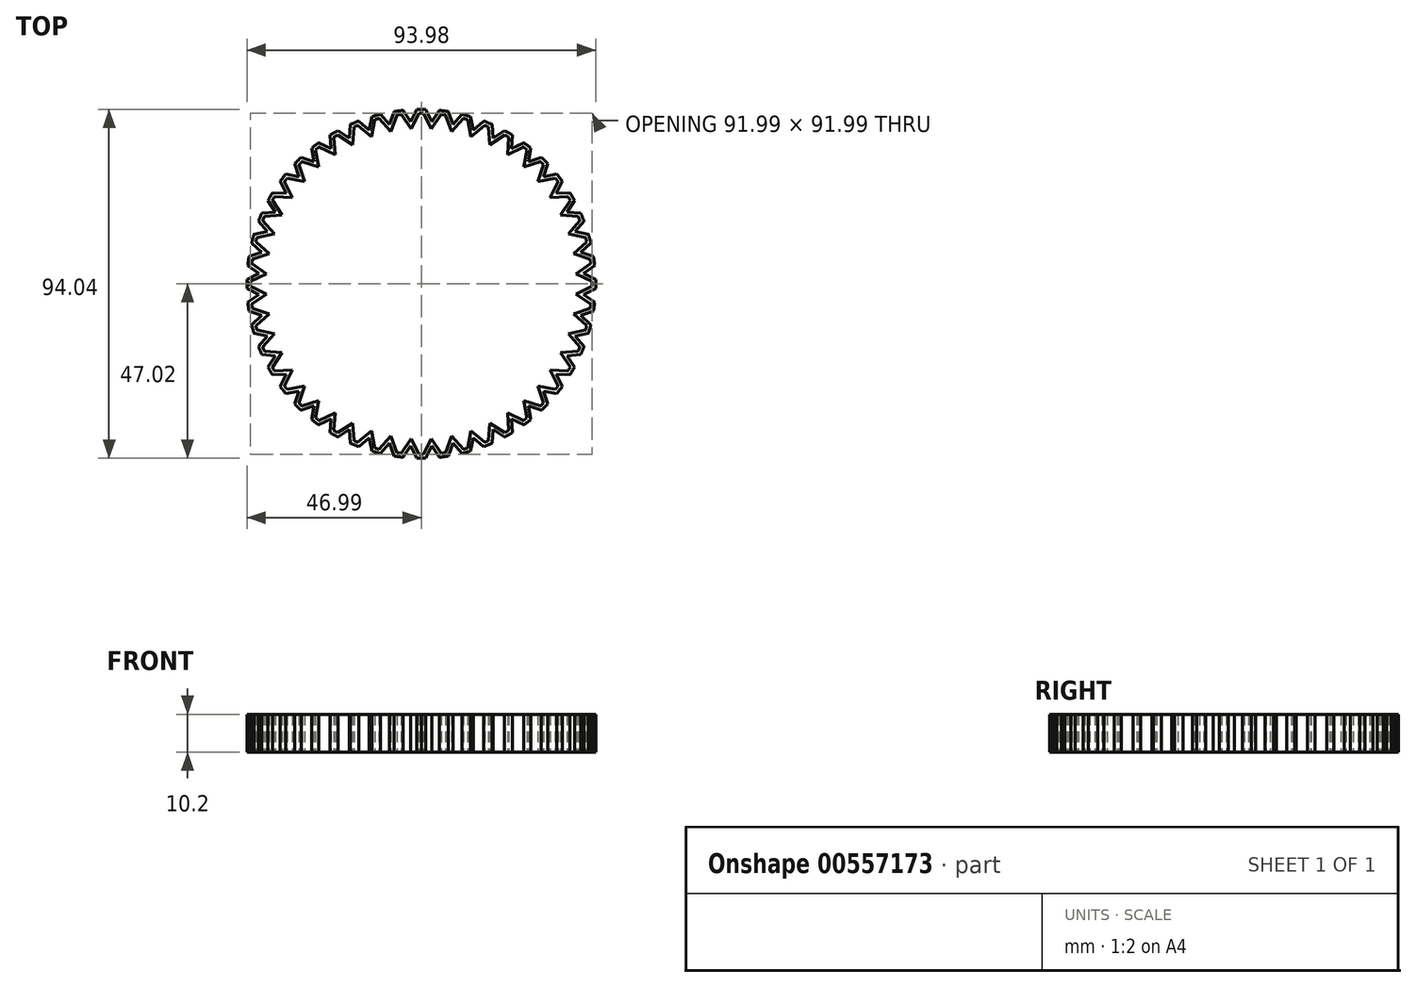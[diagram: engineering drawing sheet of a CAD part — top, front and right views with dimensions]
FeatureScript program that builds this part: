
annotation { "Feature Type Name" : "Feature", "Feature Type Description" : "" }
export const myFeature = defineFeature(function(context is Context, id is Id, definition is map)
    precondition{}
    {
        {
            var Q0;
            Q0=qCreatedBy(makeId("Top.planeOp"),FACE);
            var sketch = newSketch(context, id + "F0", { "sketchPlane" : qUnion([Q0])});
            skLineSegment(sketch, "E0", {"start": v(-43.7, 2.86) * mm, "end": v(-46.74, 4.94) * mm});
            skLineSegment(sketch, "E1", {"start": v(-46.99, 1.2) * mm, "end": v(-43.7, 2.86) * mm});
            skArc(sketch, "E2", {"start": v(-4.94, 46.74) * mm, "mid": v(-6.13, 46.6) * mm, "end": v(-7.33, 46.43) * mm});
            skArc(sketch, "E3", {"start": v(-11, 45.7) * mm, "mid": v(-12.16, 45.4) * mm, "end": v(-13.33, 45.07) * mm});
            skArc(sketch, "E4", {"start": v(-16.86, 43.87) * mm, "mid": v(-17.99, 43.42) * mm, "end": v(-19.1, 42.95) * mm});
            skArc(sketch, "E5", {"start": v(-22.45, 41.3) * mm, "mid": v(-23.5, 40.7) * mm, "end": v(-24.54, 40.09) * mm});
            skArc(sketch, "E6", {"start": v(-27.64, 38.01) * mm, "mid": v(-28.61, 37.29) * mm, "end": v(-29.56, 36.54) * mm});
            skLineSegment(sketch, "E7", {"start": v(-40.09, 24.54) * mm, "end": v(-36.42, 24.33) * mm});
            skLineSegment(sketch, "E8", {"start": v(-39.28, 19.37) * mm, "end": v(-41.3, 22.45) * mm});
            skLineSegment(sketch, "E9", {"start": v(-42.95, 19.1) * mm, "end": v(-39.28, 19.37) * mm});
            skLineSegment(sketch, "E10", {"start": v(-41.48, 14.08) * mm, "end": v(-43.87, 16.86) * mm});
            skLineSegment(sketch, "E11", {"start": v(-45.07, 13.33) * mm, "end": v(-41.48, 14.08) * mm});
            skLineSegment(sketch, "E12", {"start": v(-42.96, 8.55) * mm, "end": v(-45.7, 11) * mm});
            skLineSegment(sketch, "E13", {"start": v(-46.43, 7.33) * mm, "end": v(-42.96, 8.55) * mm});
            skLineSegment(sketch, "E14", {"start": v(-36.42, 24.33) * mm, "end": v(-38.01, 27.64) * mm});
            skLineSegment(sketch, "E15", {"start": v(-36.54, 29.56) * mm, "end": v(-32.93, 28.88) * mm});
            skLineSegment(sketch, "E16", {"start": v(-32.93, 28.88) * mm, "end": v(-34.08, 32.37) * mm});
            skLineSegment(sketch, "E17", {"start": v(-28.88, 32.93) * mm, "end": v(-32.37, 34.08) * mm});
            skLineSegment(sketch, "E18", {"start": v(-28.88, 32.93) * mm, "end": v(-29.56, 36.54) * mm});
            skLineSegment(sketch, "E19", {"start": v(-24.33, 36.42) * mm, "end": v(-27.64, 38.01) * mm});
            skLineSegment(sketch, "E20", {"start": v(-24.33, 36.42) * mm, "end": v(-24.54, 40.09) * mm});
            skLineSegment(sketch, "E21", {"start": v(-19.37, 39.28) * mm, "end": v(-22.45, 41.3) * mm});
            skLineSegment(sketch, "E22", {"start": v(-19.37, 39.28) * mm, "end": v(-19.1, 42.95) * mm});
            skLineSegment(sketch, "E23", {"start": v(-14.08, 41.48) * mm, "end": v(-16.86, 43.87) * mm});
            skLineSegment(sketch, "E24", {"start": v(-14.08, 41.48) * mm, "end": v(-13.33, 45.07) * mm});
            skLineSegment(sketch, "E25", {"start": v(-8.55, 42.96) * mm, "end": v(-11, 45.7) * mm});
            skLineSegment(sketch, "E26", {"start": v(-8.55, 42.96) * mm, "end": v(-7.33, 46.43) * mm});
            skLineSegment(sketch, "E27", {"start": v(-2.86, 43.7) * mm, "end": v(-4.94, 46.74) * mm});
            skLineSegment(sketch, "E28", {"start": v(-2.86, 43.7) * mm, "end": v(-1.2, 46.99) * mm});
            skArc(sketch, "E29", {"start": v(-46.43, 7.33) * mm, "mid": v(-46.6, 6.13) * mm, "end": v(-46.74, 4.94) * mm});
            skArc(sketch, "E30", {"start": v(-45.07, 13.33) * mm, "mid": v(-45.4, 12.16) * mm, "end": v(-45.7, 11) * mm});
            skArc(sketch, "E31", {"start": v(-42.95, 19.1) * mm, "mid": v(-43.42, 17.99) * mm, "end": v(-43.87, 16.86) * mm});
            skArc(sketch, "E32", {"start": v(-40.09, 24.54) * mm, "mid": v(-40.7, 23.5) * mm, "end": v(-41.3, 22.45) * mm});
            skArc(sketch, "E33", {"start": v(-36.54, 29.56) * mm, "mid": v(-37.29, 28.61) * mm, "end": v(-38.01, 27.64) * mm});
            skArc(sketch, "E34", {"start": v(-32.37, 34.08) * mm, "mid": v(-33.23, 33.23) * mm, "end": v(-34.08, 32.37) * mm});
            skLineSegment(sketch, "E35.0", {"start": v(-2.74, 41.75) * mm, "end": v(-0.59, 46) * mm});
            skLineSegment(sketch, "E35.1", {"start": v(-2.74, 41.75) * mm, "end": v(-5.42, 45.68) * mm});
            skArc(sketch, "E35.2", {"start": v(-5.42, 45.68) * mm, "mid": v(-6, 45.6) * mm, "end": v(-6.59, 45.53) * mm});
            skLineSegment(sketch, "E35.3", {"start": v(-8.16, 41.03) * mm, "end": v(-6.59, 45.53) * mm});
            skLineSegment(sketch, "E35.4", {"start": v(-8.16, 41.03) * mm, "end": v(-11.34, 44.58) * mm});
            skArc(sketch, "E35.5", {"start": v(-11.34, 44.58) * mm, "mid": v(-11.9, 44.43) * mm, "end": v(-12.47, 44.28) * mm});
            skLineSegment(sketch, "E35.6", {"start": v(-13.45, 39.61) * mm, "end": v(-12.47, 44.28) * mm});
            skLineSegment(sketch, "E35.7", {"start": v(-13.45, 39.61) * mm, "end": v(-17.06, 42.72) * mm});
            skArc(sketch, "E35.8", {"start": v(-17.06, 42.72) * mm, "mid": v(-17.6, 42.5) * mm, "end": v(-18.14, 42.27) * mm});
            skLineSegment(sketch, "E35.9", {"start": v(-18.5, 37.52) * mm, "end": v(-18.14, 42.27) * mm});
            skLineSegment(sketch, "E35.10", {"start": v(-18.5, 37.52) * mm, "end": v(-22.5, 40.13) * mm});
            skArc(sketch, "E35.11", {"start": v(-22.5, 40.13) * mm, "mid": v(-23, 39.84) * mm, "end": v(-23.5, 39.54) * mm});
            skLineSegment(sketch, "E35.12", {"start": v(-23.24, 34.78) * mm, "end": v(-23.5, 39.54) * mm});
            skLineSegment(sketch, "E35.13", {"start": v(-42.27, 18.14) * mm, "end": v(-37.52, 18.5) * mm});
            skArc(sketch, "E35.14", {"start": v(-42.27, 18.14) * mm, "mid": v(-42.5, 17.6) * mm, "end": v(-42.72, 17.06) * mm});
            skLineSegment(sketch, "E35.15", {"start": v(-39.61, 13.45) * mm, "end": v(-42.72, 17.06) * mm});
            skLineSegment(sketch, "E35.16", {"start": v(-44.28, 12.47) * mm, "end": v(-39.61, 13.45) * mm});
            skArc(sketch, "E35.17", {"start": v(-44.28, 12.47) * mm, "mid": v(-44.43, 11.9) * mm, "end": v(-44.58, 11.34) * mm});
            skLineSegment(sketch, "E35.18", {"start": v(-41.03, 8.16) * mm, "end": v(-44.58, 11.34) * mm});
            skLineSegment(sketch, "E35.19", {"start": v(-46, 0.59) * mm, "end": v(-41.75, 2.74) * mm});
            skLineSegment(sketch, "E35.20", {"start": v(-41.75, 2.74) * mm, "end": v(-45.68, 5.42) * mm});
            skArc(sketch, "E35.21", {"start": v(-45.53, 6.59) * mm, "mid": v(-45.6, 6) * mm, "end": v(-45.68, 5.42) * mm});
            skLineSegment(sketch, "E35.22", {"start": v(-45.53, 6.59) * mm, "end": v(-41.03, 8.16) * mm});
            skLineSegment(sketch, "E35.23", {"start": v(-37.52, 18.5) * mm, "end": v(-40.13, 22.5) * mm});
            skArc(sketch, "E35.24", {"start": v(-39.54, 23.5) * mm, "mid": v(-39.84, 23) * mm, "end": v(-40.13, 22.5) * mm});
            skLineSegment(sketch, "E35.25", {"start": v(-39.54, 23.5) * mm, "end": v(-34.78, 23.24) * mm});
            skLineSegment(sketch, "E35.26", {"start": v(-34.78, 23.24) * mm, "end": v(-36.85, 27.54) * mm});
            skArc(sketch, "E35.27", {"start": v(-36.13, 28.47) * mm, "mid": v(-36.5, 28) * mm, "end": v(-36.85, 27.54) * mm});
            skLineSegment(sketch, "E35.28", {"start": v(-36.13, 28.47) * mm, "end": v(-31.45, 27.58) * mm});
            skLineSegment(sketch, "E35.29", {"start": v(-31.45, 27.58) * mm, "end": v(-32.94, 32.1) * mm});
            skArc(sketch, "E35.30", {"start": v(-32.1, 32.94) * mm, "mid": v(-32.53, 32.53) * mm, "end": v(-32.94, 32.1) * mm});
            skLineSegment(sketch, "E35.31", {"start": v(-27.58, 31.45) * mm, "end": v(-32.1, 32.94) * mm});
            skLineSegment(sketch, "E35.32", {"start": v(-27.58, 31.45) * mm, "end": v(-28.47, 36.13) * mm});
            skArc(sketch, "E35.33", {"start": v(-27.54, 36.85) * mm, "mid": v(-28, 36.5) * mm, "end": v(-28.47, 36.13) * mm});
            skLineSegment(sketch, "E35.34", {"start": v(-23.24, 34.78) * mm, "end": v(-27.54, 36.85) * mm});
            skLineSegment(sketch, "E36", {"start": v(-0.59, 46) * mm, "end": v(0, 46) * mm});
            skLineSegment(sketch, "E37", {"start": v(-1.2, 46.99) * mm, "end": v(0, 47.02) * mm});
            skLineSegment(sketch, "E38", {"start": v(-46, 0.59) * mm, "end": v(-46, 0) * mm});
            skLineSegment(sketch, "E39", {"start": v(-46.99, 1.2) * mm, "end": v(-46.99, 0) * mm});
            skSolve(sketch);
        }
        {
            var Q0;
            Q0=qCreatedBy(makeId("Top.planeOp"),FACE);
            var sketch = newSketch(context, id + "F1", { "sketchPlane" : qUnion([Q0])});
            skLineSegment(sketch, "E40.0", {"start": v(-43.7, 2.86) * mm, "end": v(-46.74, 4.94) * mm});
            skLineSegment(sketch, "E40.1", {"start": v(-46.99, 1.2) * mm, "end": v(-43.7, 2.86) * mm});
            skArc(sketch, "E40.2", {"start": v(-4.94, 46.74) * mm, "mid": v(-6.13, 46.6) * mm, "end": v(-7.33, 46.43) * mm});
            skArc(sketch, "E40.3", {"start": v(-11, 45.7) * mm, "mid": v(-12.16, 45.4) * mm, "end": v(-13.33, 45.07) * mm});
            skArc(sketch, "E40.4", {"start": v(-16.86, 43.87) * mm, "mid": v(-17.99, 43.42) * mm, "end": v(-19.1, 42.95) * mm});
            skArc(sketch, "E40.5", {"start": v(-22.45, 41.3) * mm, "mid": v(-23.5, 40.7) * mm, "end": v(-24.54, 40.09) * mm});
            skArc(sketch, "E40.6", {"start": v(-27.64, 38.01) * mm, "mid": v(-28.61, 37.29) * mm, "end": v(-29.56, 36.54) * mm});
            skLineSegment(sketch, "E40.7", {"start": v(-40.09, 24.54) * mm, "end": v(-36.42, 24.33) * mm});
            skLineSegment(sketch, "E40.8", {"start": v(-39.28, 19.37) * mm, "end": v(-41.3, 22.45) * mm});
            skLineSegment(sketch, "E40.9", {"start": v(-42.95, 19.1) * mm, "end": v(-39.28, 19.37) * mm});
            skLineSegment(sketch, "E40.10", {"start": v(-41.48, 14.08) * mm, "end": v(-43.87, 16.86) * mm});
            skLineSegment(sketch, "E40.11", {"start": v(-45.07, 13.33) * mm, "end": v(-41.48, 14.08) * mm});
            skLineSegment(sketch, "E40.12", {"start": v(-42.96, 8.55) * mm, "end": v(-45.7, 11) * mm});
            skLineSegment(sketch, "E40.13", {"start": v(-46.43, 7.33) * mm, "end": v(-42.96, 8.55) * mm});
            skLineSegment(sketch, "E40.14", {"start": v(-36.42, 24.33) * mm, "end": v(-38.01, 27.64) * mm});
            skLineSegment(sketch, "E40.15", {"start": v(-36.54, 29.56) * mm, "end": v(-32.93, 28.88) * mm});
            skLineSegment(sketch, "E40.16", {"start": v(-32.93, 28.88) * mm, "end": v(-34.08, 32.37) * mm});
            skLineSegment(sketch, "E40.17", {"start": v(-28.88, 32.93) * mm, "end": v(-32.37, 34.08) * mm});
            skLineSegment(sketch, "E40.18", {"start": v(-28.88, 32.93) * mm, "end": v(-29.56, 36.54) * mm});
            skLineSegment(sketch, "E40.19", {"start": v(-24.33, 36.42) * mm, "end": v(-27.64, 38.01) * mm});
            skLineSegment(sketch, "E40.20", {"start": v(-24.33, 36.42) * mm, "end": v(-24.54, 40.09) * mm});
            skLineSegment(sketch, "E40.21", {"start": v(-19.37, 39.28) * mm, "end": v(-22.45, 41.3) * mm});
            skLineSegment(sketch, "E40.22", {"start": v(-19.37, 39.28) * mm, "end": v(-19.1, 42.95) * mm});
            skLineSegment(sketch, "E40.23", {"start": v(-14.08, 41.48) * mm, "end": v(-16.86, 43.87) * mm});
            skLineSegment(sketch, "E40.24", {"start": v(-14.08, 41.48) * mm, "end": v(-13.33, 45.07) * mm});
            skLineSegment(sketch, "E40.25", {"start": v(-8.55, 42.96) * mm, "end": v(-11, 45.7) * mm});
            skLineSegment(sketch, "E40.26", {"start": v(-8.55, 42.96) * mm, "end": v(-7.33, 46.43) * mm});
            skLineSegment(sketch, "E40.27", {"start": v(-2.86, 43.7) * mm, "end": v(-4.94, 46.74) * mm});
            skLineSegment(sketch, "E40.28", {"start": v(-2.86, 43.7) * mm, "end": v(-1.2, 46.99) * mm});
            skArc(sketch, "E40.29", {"start": v(-46.43, 7.33) * mm, "mid": v(-46.6, 6.13) * mm, "end": v(-46.74, 4.94) * mm});
            skArc(sketch, "E40.30", {"start": v(-45.07, 13.33) * mm, "mid": v(-45.4, 12.16) * mm, "end": v(-45.7, 11) * mm});
            skArc(sketch, "E40.31", {"start": v(-42.95, 19.1) * mm, "mid": v(-43.42, 17.99) * mm, "end": v(-43.87, 16.86) * mm});
            skArc(sketch, "E40.32", {"start": v(-40.09, 24.54) * mm, "mid": v(-40.7, 23.5) * mm, "end": v(-41.3, 22.45) * mm});
            skArc(sketch, "E40.33", {"start": v(-36.54, 29.56) * mm, "mid": v(-37.29, 28.61) * mm, "end": v(-38.01, 27.64) * mm});
            skArc(sketch, "E40.34", {"start": v(-32.37, 34.08) * mm, "mid": v(-33.23, 33.23) * mm, "end": v(-34.08, 32.37) * mm});
            skLineSegment(sketch, "E40.35", {"start": v(-2.74, 41.75) * mm, "end": v(-0.59, 46) * mm});
            skLineSegment(sketch, "E40.36", {"start": v(-2.74, 41.75) * mm, "end": v(-5.42, 45.68) * mm});
            skArc(sketch, "E40.37", {"start": v(-5.42, 45.68) * mm, "mid": v(-6, 45.6) * mm, "end": v(-6.59, 45.53) * mm});
            skLineSegment(sketch, "E40.38", {"start": v(-8.16, 41.03) * mm, "end": v(-6.59, 45.53) * mm});
            skLineSegment(sketch, "E40.39", {"start": v(-8.16, 41.03) * mm, "end": v(-11.34, 44.58) * mm});
            skArc(sketch, "E40.40", {"start": v(-11.34, 44.58) * mm, "mid": v(-11.9, 44.43) * mm, "end": v(-12.47, 44.28) * mm});
            skLineSegment(sketch, "E40.41", {"start": v(-13.45, 39.61) * mm, "end": v(-12.47, 44.28) * mm});
            skLineSegment(sketch, "E40.42", {"start": v(-13.45, 39.61) * mm, "end": v(-17.06, 42.72) * mm});
            skArc(sketch, "E40.43", {"start": v(-17.06, 42.72) * mm, "mid": v(-17.6, 42.5) * mm, "end": v(-18.14, 42.27) * mm});
            skLineSegment(sketch, "E40.44", {"start": v(-18.5, 37.52) * mm, "end": v(-18.14, 42.27) * mm});
            skLineSegment(sketch, "E40.45", {"start": v(-18.5, 37.52) * mm, "end": v(-22.5, 40.13) * mm});
            skArc(sketch, "E40.46", {"start": v(-22.5, 40.13) * mm, "mid": v(-23, 39.84) * mm, "end": v(-23.5, 39.54) * mm});
            skLineSegment(sketch, "E40.47", {"start": v(-23.24, 34.78) * mm, "end": v(-23.5, 39.54) * mm});
            skLineSegment(sketch, "E40.48", {"start": v(-42.27, 18.14) * mm, "end": v(-37.52, 18.5) * mm});
            skArc(sketch, "E40.49", {"start": v(-42.27, 18.14) * mm, "mid": v(-42.5, 17.6) * mm, "end": v(-42.72, 17.06) * mm});
            skLineSegment(sketch, "E40.50", {"start": v(-39.61, 13.45) * mm, "end": v(-42.72, 17.06) * mm});
            skLineSegment(sketch, "E40.51", {"start": v(-44.28, 12.47) * mm, "end": v(-39.61, 13.45) * mm});
            skArc(sketch, "E40.52", {"start": v(-44.28, 12.47) * mm, "mid": v(-44.43, 11.9) * mm, "end": v(-44.58, 11.34) * mm});
            skLineSegment(sketch, "E40.53", {"start": v(-41.03, 8.16) * mm, "end": v(-44.58, 11.34) * mm});
            skLineSegment(sketch, "E40.54", {"start": v(-46, 0.59) * mm, "end": v(-41.75, 2.74) * mm});
            skLineSegment(sketch, "E40.55", {"start": v(-41.75, 2.74) * mm, "end": v(-45.68, 5.42) * mm});
            skArc(sketch, "E40.56", {"start": v(-45.53, 6.59) * mm, "mid": v(-45.6, 6) * mm, "end": v(-45.68, 5.42) * mm});
            skLineSegment(sketch, "E40.57", {"start": v(-45.53, 6.59) * mm, "end": v(-41.03, 8.16) * mm});
            skLineSegment(sketch, "E40.58", {"start": v(-37.52, 18.5) * mm, "end": v(-40.13, 22.5) * mm});
            skArc(sketch, "E40.59", {"start": v(-39.54, 23.5) * mm, "mid": v(-39.84, 23) * mm, "end": v(-40.13, 22.5) * mm});
            skLineSegment(sketch, "E40.60", {"start": v(-39.54, 23.5) * mm, "end": v(-34.78, 23.24) * mm});
            skLineSegment(sketch, "E40.61", {"start": v(-34.78, 23.24) * mm, "end": v(-36.85, 27.54) * mm});
            skArc(sketch, "E40.62", {"start": v(-36.13, 28.47) * mm, "mid": v(-36.5, 28) * mm, "end": v(-36.85, 27.54) * mm});
            skLineSegment(sketch, "E40.63", {"start": v(-36.13, 28.47) * mm, "end": v(-31.45, 27.58) * mm});
            skLineSegment(sketch, "E40.64", {"start": v(-31.45, 27.58) * mm, "end": v(-32.94, 32.1) * mm});
            skArc(sketch, "E40.65", {"start": v(-32.1, 32.94) * mm, "mid": v(-32.53, 32.53) * mm, "end": v(-32.94, 32.1) * mm});
            skLineSegment(sketch, "E40.66", {"start": v(-27.58, 31.45) * mm, "end": v(-32.1, 32.94) * mm});
            skLineSegment(sketch, "E40.67", {"start": v(-27.58, 31.45) * mm, "end": v(-28.47, 36.13) * mm});
            skArc(sketch, "E40.68", {"start": v(-27.54, 36.85) * mm, "mid": v(-28, 36.5) * mm, "end": v(-28.47, 36.13) * mm});
            skLineSegment(sketch, "E40.69", {"start": v(-23.24, 34.78) * mm, "end": v(-27.54, 36.85) * mm});
            skLineSegment(sketch, "E40.70", {"start": v(-0.59, 46) * mm, "end": v(0, 46) * mm});
            skLineSegment(sketch, "E40.71", {"start": v(-1.2, 46.99) * mm, "end": v(0, 47.02) * mm});
            skLineSegment(sketch, "E40.72", {"start": v(-46, 0.59) * mm, "end": v(-46, 0) * mm});
            skLineSegment(sketch, "E40.73", {"start": v(-46.99, 1.2) * mm, "end": v(-46.99, 0) * mm});
            skArc(sketch, "E41.MirrorCS", {"start": v(17.06, 42.72) * mm, "mid": v(17.6, 42.5) * mm, "end": v(18.14, 42.27) * mm});
            skArc(sketch, "E42.MirrorCS", {"start": v(39.54, 23.5) * mm, "mid": v(39.84, 23) * mm, "end": v(40.13, 22.5) * mm});
            skLineSegment(sketch, "E43.MirrorCS", {"start": v(1.2, 46.99) * mm, "end": v(0, 47.02) * mm});
            skArc(sketch, "E44.MirrorCS", {"start": v(27.54, 36.85) * mm, "mid": v(28, 36.5) * mm, "end": v(28.47, 36.13) * mm});
            skArc(sketch, "E45.MirrorCS", {"start": v(44.28, 12.47) * mm, "mid": v(44.43, 11.9) * mm, "end": v(44.58, 11.34) * mm});
            skArc(sketch, "E46.MirrorCS", {"start": v(11, 45.7) * mm, "mid": v(12.16, 45.4) * mm, "end": v(13.33, 45.07) * mm});
            skArc(sketch, "E47.MirrorCS", {"start": v(16.86, 43.87) * mm, "mid": v(17.99, 43.42) * mm, "end": v(19.1, 42.95) * mm});
            skArc(sketch, "E48.MirrorCS", {"start": v(22.45, 41.3) * mm, "mid": v(23.5, 40.7) * mm, "end": v(24.54, 40.09) * mm});
            skArc(sketch, "E49.MirrorCS", {"start": v(27.64, 38.01) * mm, "mid": v(28.61, 37.29) * mm, "end": v(29.56, 36.54) * mm});
            skArc(sketch, "E50.MirrorCS", {"start": v(40.09, 24.54) * mm, "mid": v(40.7, 23.5) * mm, "end": v(41.3, 22.45) * mm});
            skLineSegment(sketch, "E51.MirrorCS", {"start": v(46, 0.59) * mm, "end": v(46, 0) * mm});
            skArc(sketch, "E52.MirrorCS", {"start": v(11.34, 44.58) * mm, "mid": v(11.9, 44.43) * mm, "end": v(12.47, 44.28) * mm});
            skArc(sketch, "E53.MirrorCS", {"start": v(45.53, 6.59) * mm, "mid": v(45.6, 6) * mm, "end": v(45.68, 5.42) * mm});
            skArc(sketch, "E54.MirrorCS", {"start": v(36.13, 28.47) * mm, "mid": v(36.5, 28) * mm, "end": v(36.85, 27.54) * mm});
            skArc(sketch, "E55.MirrorCS", {"start": v(22.5, 40.13) * mm, "mid": v(23, 39.84) * mm, "end": v(23.5, 39.54) * mm});
            skArc(sketch, "E56.MirrorCS", {"start": v(45.07, 13.33) * mm, "mid": v(45.4, 12.16) * mm, "end": v(45.7, 11) * mm});
            skArc(sketch, "E57.MirrorCS", {"start": v(5.42, 45.68) * mm, "mid": v(6, 45.6) * mm, "end": v(6.59, 45.53) * mm});
            skArc(sketch, "E58.MirrorCS", {"start": v(32.1, 32.94) * mm, "mid": v(32.53, 32.53) * mm, "end": v(32.94, 32.1) * mm});
            skArc(sketch, "E59.MirrorCS", {"start": v(42.27, 18.14) * mm, "mid": v(42.5, 17.6) * mm, "end": v(42.72, 17.06) * mm});
            skArc(sketch, "E60.MirrorCS", {"start": v(36.54, 29.56) * mm, "mid": v(37.29, 28.61) * mm, "end": v(38.01, 27.64) * mm});
            skLineSegment(sketch, "E61.MirrorCS", {"start": v(46.99, 1.2) * mm, "end": v(46.99, 0) * mm});
            skLineSegment(sketch, "E62.MirrorCS", {"start": v(0.59, 46) * mm, "end": v(0, 46) * mm});
            skArc(sketch, "E63.MirrorCS", {"start": v(42.95, 19.1) * mm, "mid": v(43.42, 17.99) * mm, "end": v(43.87, 16.86) * mm});
            skArc(sketch, "E64.MirrorCS", {"start": v(32.37, 34.08) * mm, "mid": v(33.23, 33.23) * mm, "end": v(34.08, 32.37) * mm});
            skLineSegment(sketch, "E65.MirrorCS", {"start": v(13.45, 39.61) * mm, "end": v(17.06, 42.72) * mm});
            skLineSegment(sketch, "E66.MirrorCS", {"start": v(37.52, 18.5) * mm, "end": v(40.13, 22.5) * mm});
            skLineSegment(sketch, "E67.MirrorCS", {"start": v(27.58, 31.45) * mm, "end": v(28.47, 36.13) * mm});
            skLineSegment(sketch, "E68.MirrorCS", {"start": v(24.33, 36.42) * mm, "end": v(27.64, 38.01) * mm});
            skLineSegment(sketch, "E69.MirrorCS", {"start": v(2.86, 43.7) * mm, "end": v(4.94, 46.74) * mm});
            skLineSegment(sketch, "E70.MirrorCS", {"start": v(8.16, 41.03) * mm, "end": v(11.34, 44.58) * mm});
            skLineSegment(sketch, "E71.MirrorCS", {"start": v(36.42, 24.33) * mm, "end": v(38.01, 27.64) * mm});
            skLineSegment(sketch, "E72.MirrorCS", {"start": v(14.08, 41.48) * mm, "end": v(16.86, 43.87) * mm});
            skLineSegment(sketch, "E73.MirrorCS", {"start": v(36.54, 29.56) * mm, "end": v(32.93, 28.88) * mm});
            skLineSegment(sketch, "E74.MirrorCS", {"start": v(43.7, 2.86) * mm, "end": v(46.74, 4.94) * mm});
            skArc(sketch, "E75.MirrorCS", {"start": v(4.94, 46.74) * mm, "mid": v(6.13, 46.6) * mm, "end": v(7.33, 46.43) * mm});
            skLineSegment(sketch, "E76.MirrorCS", {"start": v(34.78, 23.24) * mm, "end": v(36.85, 27.54) * mm});
            skLineSegment(sketch, "E77.MirrorCS", {"start": v(18.5, 37.52) * mm, "end": v(22.5, 40.13) * mm});
            skArc(sketch, "E78.MirrorCS", {"start": v(46.43, 7.33) * mm, "mid": v(46.6, 6.13) * mm, "end": v(46.74, 4.94) * mm});
            skLineSegment(sketch, "E79.MirrorCS", {"start": v(24.33, 36.42) * mm, "end": v(24.54, 40.09) * mm});
            skLineSegment(sketch, "E80.MirrorCS", {"start": v(31.45, 27.58) * mm, "end": v(32.94, 32.1) * mm});
            skLineSegment(sketch, "E81.MirrorCS", {"start": v(42.27, 18.14) * mm, "end": v(37.52, 18.5) * mm});
            skLineSegment(sketch, "E82.MirrorCS", {"start": v(32.93, 28.88) * mm, "end": v(34.08, 32.37) * mm});
            skLineSegment(sketch, "E83.MirrorCS", {"start": v(40.09, 24.54) * mm, "end": v(36.42, 24.33) * mm});
            skLineSegment(sketch, "E84.MirrorCS", {"start": v(39.28, 19.37) * mm, "end": v(41.3, 22.45) * mm});
            skLineSegment(sketch, "E85.MirrorCS", {"start": v(42.95, 19.1) * mm, "end": v(39.28, 19.37) * mm});
            skLineSegment(sketch, "E86.MirrorCS", {"start": v(41.48, 14.08) * mm, "end": v(43.87, 16.86) * mm});
            skLineSegment(sketch, "E87.MirrorCS", {"start": v(42.96, 8.55) * mm, "end": v(45.7, 11) * mm});
            skLineSegment(sketch, "E88.MirrorCS", {"start": v(18.5, 37.52) * mm, "end": v(18.14, 42.27) * mm});
            skLineSegment(sketch, "E89.MirrorCS", {"start": v(39.54, 23.5) * mm, "end": v(34.78, 23.24) * mm});
            skLineSegment(sketch, "E90.MirrorCS", {"start": v(14.08, 41.48) * mm, "end": v(13.33, 45.07) * mm});
            skLineSegment(sketch, "E91.MirrorCS", {"start": v(23.24, 34.78) * mm, "end": v(27.54, 36.85) * mm});
            skLineSegment(sketch, "E92.MirrorCS", {"start": v(41.03, 8.16) * mm, "end": v(44.58, 11.34) * mm});
            skLineSegment(sketch, "E93.MirrorCS", {"start": v(19.37, 39.28) * mm, "end": v(22.45, 41.3) * mm});
            skLineSegment(sketch, "E94.MirrorCS", {"start": v(28.88, 32.93) * mm, "end": v(32.37, 34.08) * mm});
            skLineSegment(sketch, "E95.MirrorCS", {"start": v(8.55, 42.96) * mm, "end": v(11, 45.7) * mm});
            skLineSegment(sketch, "E96.MirrorCS", {"start": v(36.13, 28.47) * mm, "end": v(31.45, 27.58) * mm});
            skLineSegment(sketch, "E97.MirrorCS", {"start": v(23.24, 34.78) * mm, "end": v(23.5, 39.54) * mm});
            skLineSegment(sketch, "E98.MirrorCS", {"start": v(19.37, 39.28) * mm, "end": v(19.1, 42.95) * mm});
            skLineSegment(sketch, "E99.MirrorCS", {"start": v(27.58, 31.45) * mm, "end": v(32.1, 32.94) * mm});
            skLineSegment(sketch, "E100.MirrorCS", {"start": v(39.61, 13.45) * mm, "end": v(42.72, 17.06) * mm});
            skLineSegment(sketch, "E101.MirrorCS", {"start": v(28.88, 32.93) * mm, "end": v(29.56, 36.54) * mm});
            skLineSegment(sketch, "E102.MirrorCS", {"start": v(44.28, 12.47) * mm, "end": v(39.61, 13.45) * mm});
            skLineSegment(sketch, "E103.MirrorCS", {"start": v(8.55, 42.96) * mm, "end": v(7.33, 46.43) * mm});
            skLineSegment(sketch, "E104.MirrorCS", {"start": v(2.74, 41.75) * mm, "end": v(0.59, 46) * mm});
            skLineSegment(sketch, "E105.MirrorCS", {"start": v(46.43, 7.33) * mm, "end": v(42.96, 8.55) * mm});
            skLineSegment(sketch, "E106.MirrorCS", {"start": v(41.75, 2.74) * mm, "end": v(45.68, 5.42) * mm});
            skLineSegment(sketch, "E107.MirrorCS", {"start": v(46.99, 1.2) * mm, "end": v(43.7, 2.86) * mm});
            skLineSegment(sketch, "E108.MirrorCS", {"start": v(2.74, 41.75) * mm, "end": v(5.42, 45.68) * mm});
            skLineSegment(sketch, "E109.MirrorCS", {"start": v(45.07, 13.33) * mm, "end": v(41.48, 14.08) * mm});
            skLineSegment(sketch, "E110.MirrorCS", {"start": v(2.86, 43.7) * mm, "end": v(1.2, 46.99) * mm});
            skLineSegment(sketch, "E111.MirrorCS", {"start": v(13.45, 39.61) * mm, "end": v(12.47, 44.28) * mm});
            skLineSegment(sketch, "E112.MirrorCS", {"start": v(45.53, 6.59) * mm, "end": v(41.03, 8.16) * mm});
            skLineSegment(sketch, "E113.MirrorCS", {"start": v(8.16, 41.03) * mm, "end": v(6.59, 45.53) * mm});
            skLineSegment(sketch, "E114.MirrorCS", {"start": v(46, 0.59) * mm, "end": v(41.75, 2.74) * mm});
            skLineSegment(sketch, "E115.MirrorCS", {"start": v(-46, -0.59) * mm, "end": v(-46, 0) * mm});
            skLineSegment(sketch, "E116.MirrorCS", {"start": v(-46.99, -1.2) * mm, "end": v(-46.99, 0) * mm});
            skArc(sketch, "E117.MirrorCS", {"start": v(-46.43, -7.33) * mm, "mid": v(-46.6, -6.13) * mm, "end": v(-46.74, -4.94) * mm});
            skArc(sketch, "E118.MirrorCS", {"start": v(-44.28, -12.47) * mm, "mid": v(-44.43, -11.9) * mm, "end": v(-44.58, -11.34) * mm});
            skArc(sketch, "E119.MirrorCS", {"start": v(-27.54, -36.85) * mm, "mid": v(-28, -36.5) * mm, "end": v(-28.47, -36.13) * mm});
            skArc(sketch, "E120.MirrorCS", {"start": v(-39.54, -23.5) * mm, "mid": v(-39.84, -23) * mm, "end": v(-40.13, -22.5) * mm});
            skArc(sketch, "E121.MirrorCS", {"start": v(-17.06, -42.72) * mm, "mid": v(-17.6, -42.5) * mm, "end": v(-18.14, -42.27) * mm});
            skArc(sketch, "E122.MirrorCS", {"start": v(-45.07, -13.33) * mm, "mid": v(-45.4, -12.16) * mm, "end": v(-45.7, -11) * mm});
            skArc(sketch, "E123.MirrorCS", {"start": v(-5.42, -45.68) * mm, "mid": v(-6, -45.6) * mm, "end": v(-6.59, -45.53) * mm});
            skArc(sketch, "E124.MirrorCS", {"start": v(-22.5, -40.13) * mm, "mid": v(-23, -39.84) * mm, "end": v(-23.5, -39.54) * mm});
            skArc(sketch, "E125.MirrorCS", {"start": v(-36.13, -28.47) * mm, "mid": v(-36.5, -28) * mm, "end": v(-36.85, -27.54) * mm});
            skLineSegment(sketch, "E126.MirrorCS", {"start": v(-0.59, -46) * mm, "end": v(0, -46) * mm});
            skArc(sketch, "E127.MirrorCS", {"start": v(-42.95, -19.1) * mm, "mid": v(-43.42, -17.99) * mm, "end": v(-43.87, -16.86) * mm});
            skLineSegment(sketch, "E128.MirrorCS", {"start": v(-1.2, -46.99) * mm, "end": v(0, -47.02) * mm});
            skArc(sketch, "E129.MirrorCS", {"start": v(-22.45, -41.3) * mm, "mid": v(-23.5, -40.7) * mm, "end": v(-24.54, -40.09) * mm});
            skArc(sketch, "E130.MirrorCS", {"start": v(-27.64, -38.01) * mm, "mid": v(-28.61, -37.29) * mm, "end": v(-29.56, -36.54) * mm});
            skArc(sketch, "E131.MirrorCS", {"start": v(-40.09, -24.54) * mm, "mid": v(-40.7, -23.5) * mm, "end": v(-41.3, -22.45) * mm});
            skArc(sketch, "E132.MirrorCS", {"start": v(-11.34, -44.58) * mm, "mid": v(-11.9, -44.43) * mm, "end": v(-12.47, -44.28) * mm});
            skArc(sketch, "E133.MirrorCS", {"start": v(-45.53, -6.59) * mm, "mid": v(-45.6, -6) * mm, "end": v(-45.68, -5.42) * mm});
            skArc(sketch, "E134.MirrorCS", {"start": v(-32.1, -32.94) * mm, "mid": v(-32.53, -32.53) * mm, "end": v(-32.94, -32.1) * mm});
            skArc(sketch, "E135.MirrorCS", {"start": v(-42.27, -18.14) * mm, "mid": v(-42.5, -17.6) * mm, "end": v(-42.72, -17.06) * mm});
            skLineSegment(sketch, "E136.MirrorCS", {"start": v(0.59, -46) * mm, "end": v(0, -46) * mm});
            skLineSegment(sketch, "E137.MirrorCS", {"start": v(2.74, -41.75) * mm, "end": v(5.42, -45.68) * mm});
            skArc(sketch, "E138.MirrorCS", {"start": v(27.54, -36.85) * mm, "mid": v(28, -36.5) * mm, "end": v(28.47, -36.13) * mm});
            skLineSegment(sketch, "E139.MirrorCS", {"start": v(46, -0.59) * mm, "end": v(46, 0) * mm});
            skLineSegment(sketch, "E140.MirrorCS", {"start": v(27.58, -31.45) * mm, "end": v(28.47, -36.13) * mm});
            skArc(sketch, "E141.MirrorCS", {"start": v(36.54, -29.56) * mm, "mid": v(37.29, -28.61) * mm, "end": v(38.01, -27.64) * mm});
            skLineSegment(sketch, "E142.MirrorCS", {"start": v(34.78, -23.24) * mm, "end": v(36.85, -27.54) * mm});
            skLineSegment(sketch, "E143.MirrorCS", {"start": v(27.58, -31.45) * mm, "end": v(32.1, -32.94) * mm});
            skLineSegment(sketch, "E144.MirrorCS", {"start": v(40.09, -24.54) * mm, "end": v(36.42, -24.33) * mm});
            skLineSegment(sketch, "E145.MirrorCS", {"start": v(41.03, -8.16) * mm, "end": v(44.58, -11.34) * mm});
            skLineSegment(sketch, "E146.MirrorCS", {"start": v(-24.33, -36.42) * mm, "end": v(-24.54, -40.09) * mm});
            skLineSegment(sketch, "E147.MirrorCS", {"start": v(-18.5, -37.52) * mm, "end": v(-22.5, -40.13) * mm});
            skArc(sketch, "E148.MirrorCS", {"start": v(11.34, -44.58) * mm, "mid": v(11.9, -44.43) * mm, "end": v(12.47, -44.28) * mm});
            skLineSegment(sketch, "E149.MirrorCS", {"start": v(24.33, -36.42) * mm, "end": v(27.64, -38.01) * mm});
            skArc(sketch, "E150.MirrorCS", {"start": v(44.28, -12.47) * mm, "mid": v(44.43, -11.9) * mm, "end": v(44.58, -11.34) * mm});
            skLineSegment(sketch, "E151.MirrorCS", {"start": v(46.99, -1.2) * mm, "end": v(46.99, 0) * mm});
            skLineSegment(sketch, "E152.MirrorCS", {"start": v(18.5, -37.52) * mm, "end": v(22.5, -40.13) * mm});
            skLineSegment(sketch, "E153.MirrorCS", {"start": v(-34.78, -23.24) * mm, "end": v(-36.85, -27.54) * mm});
            skLineSegment(sketch, "E154.MirrorCS", {"start": v(39.28, -19.37) * mm, "end": v(41.3, -22.45) * mm});
            skLineSegment(sketch, "E155.MirrorCS", {"start": v(39.61, -13.45) * mm, "end": v(42.72, -17.06) * mm});
            skLineSegment(sketch, "E156.MirrorCS", {"start": v(41.75, -2.74) * mm, "end": v(45.68, -5.42) * mm});
            skLineSegment(sketch, "E157.MirrorCS", {"start": v(14.08, -41.48) * mm, "end": v(13.33, -45.07) * mm});
            skLineSegment(sketch, "E158.MirrorCS", {"start": v(43.7, -2.86) * mm, "end": v(46.74, -4.94) * mm});
            skArc(sketch, "E159.MirrorCS", {"start": v(32.1, -32.94) * mm, "mid": v(32.53, -32.53) * mm, "end": v(32.94, -32.1) * mm});
            skArc(sketch, "E160.MirrorCS", {"start": v(39.54, -23.5) * mm, "mid": v(39.84, -23) * mm, "end": v(40.13, -22.5) * mm});
            skLineSegment(sketch, "E161.MirrorCS", {"start": v(-2.86, -43.7) * mm, "end": v(-4.94, -46.74) * mm});
            skLineSegment(sketch, "E162.MirrorCS", {"start": v(19.37, -39.28) * mm, "end": v(22.45, -41.3) * mm});
            skLineSegment(sketch, "E163.MirrorCS", {"start": v(-19.37, -39.28) * mm, "end": v(-22.45, -41.3) * mm});
            skLineSegment(sketch, "E164.MirrorCS", {"start": v(-41.03, -8.16) * mm, "end": v(-44.58, -11.34) * mm});
            skLineSegment(sketch, "E165.MirrorCS", {"start": v(-23.24, -34.78) * mm, "end": v(-27.54, -36.85) * mm});
            skLineSegment(sketch, "E166.MirrorCS", {"start": v(23.24, -34.78) * mm, "end": v(27.54, -36.85) * mm});
            skLineSegment(sketch, "E167.MirrorCS", {"start": v(-39.54, -23.5) * mm, "end": v(-34.78, -23.24) * mm});
            skLineSegment(sketch, "E168.MirrorCS", {"start": v(1.2, -46.99) * mm, "end": v(0, -47.02) * mm});
            skArc(sketch, "E169.MirrorCS", {"start": v(42.27, -18.14) * mm, "mid": v(42.5, -17.6) * mm, "end": v(42.72, -17.06) * mm});
            skArc(sketch, "E170.MirrorCS", {"start": v(4.94, -46.74) * mm, "mid": v(6.13, -46.6) * mm, "end": v(7.33, -46.43) * mm});
            skLineSegment(sketch, "E171.MirrorCS", {"start": v(-18.5, -37.52) * mm, "end": v(-18.14, -42.27) * mm});
            skArc(sketch, "E172.MirrorCS", {"start": v(40.09, -24.54) * mm, "mid": v(40.7, -23.5) * mm, "end": v(41.3, -22.45) * mm});
            skLineSegment(sketch, "E173.MirrorCS", {"start": v(37.52, -18.5) * mm, "end": v(40.13, -22.5) * mm});
            skLineSegment(sketch, "E174.MirrorCS", {"start": v(32.93, -28.88) * mm, "end": v(34.08, -32.37) * mm});
            skLineSegment(sketch, "E175.MirrorCS", {"start": v(19.37, -39.28) * mm, "end": v(19.1, -42.95) * mm});
            skLineSegment(sketch, "E176.MirrorCS", {"start": v(-24.33, -36.42) * mm, "end": v(-27.64, -38.01) * mm});
            skLineSegment(sketch, "E177.MirrorCS", {"start": v(-2.74, -41.75) * mm, "end": v(-0.59, -46) * mm});
            skLineSegment(sketch, "E178.MirrorCS", {"start": v(-44.28, -12.47) * mm, "end": v(-39.61, -13.45) * mm});
            skLineSegment(sketch, "E179.MirrorCS", {"start": v(-27.58, -31.45) * mm, "end": v(-28.47, -36.13) * mm});
            skLineSegment(sketch, "E180.MirrorCS", {"start": v(46.43, -7.33) * mm, "end": v(42.96, -8.55) * mm});
            skLineSegment(sketch, "E181.MirrorCS", {"start": v(39.54, -23.5) * mm, "end": v(34.78, -23.24) * mm});
            skLineSegment(sketch, "E182.MirrorCS", {"start": v(-37.52, -18.5) * mm, "end": v(-40.13, -22.5) * mm});
            skArc(sketch, "E183.MirrorCS", {"start": v(17.06, -42.72) * mm, "mid": v(17.6, -42.5) * mm, "end": v(18.14, -42.27) * mm});
            skArc(sketch, "E184.MirrorCS", {"start": v(5.42, -45.68) * mm, "mid": v(6, -45.6) * mm, "end": v(6.59, -45.53) * mm});
            skLineSegment(sketch, "E185.MirrorCS", {"start": v(-8.55, -42.96) * mm, "end": v(-7.33, -46.43) * mm});
            skLineSegment(sketch, "E186.MirrorCS", {"start": v(-13.45, -39.61) * mm, "end": v(-17.06, -42.72) * mm});
            skLineSegment(sketch, "E187.MirrorCS", {"start": v(-8.16, -41.03) * mm, "end": v(-6.59, -45.53) * mm});
            skLineSegment(sketch, "E188.MirrorCS", {"start": v(-23.24, -34.78) * mm, "end": v(-23.5, -39.54) * mm});
            skLineSegment(sketch, "E189.MirrorCS", {"start": v(-19.37, -39.28) * mm, "end": v(-19.1, -42.95) * mm});
            skLineSegment(sketch, "E190.MirrorCS", {"start": v(28.88, -32.93) * mm, "end": v(29.56, -36.54) * mm});
            skArc(sketch, "E191.MirrorCS", {"start": v(46.43, -7.33) * mm, "mid": v(46.6, -6.13) * mm, "end": v(46.74, -4.94) * mm});
            skLineSegment(sketch, "E192.MirrorCS", {"start": v(28.88, -32.93) * mm, "end": v(32.37, -34.08) * mm});
            skLineSegment(sketch, "E193.MirrorCS", {"start": v(42.95, -19.1) * mm, "end": v(39.28, -19.37) * mm});
            skArc(sketch, "E194.MirrorCS", {"start": v(11, -45.7) * mm, "mid": v(12.16, -45.4) * mm, "end": v(13.33, -45.07) * mm});
            skLineSegment(sketch, "E195.MirrorCS", {"start": v(2.86, -43.7) * mm, "end": v(4.94, -46.74) * mm});
            skArc(sketch, "E196.MirrorCS", {"start": v(45.53, -6.59) * mm, "mid": v(45.6, -6) * mm, "end": v(45.68, -5.42) * mm});
            skLineSegment(sketch, "E197.MirrorCS", {"start": v(8.55, -42.96) * mm, "end": v(11, -45.7) * mm});
            skLineSegment(sketch, "E198.MirrorCS", {"start": v(24.33, -36.42) * mm, "end": v(24.54, -40.09) * mm});
            skArc(sketch, "E199.MirrorCS", {"start": v(42.95, -19.1) * mm, "mid": v(43.42, -17.99) * mm, "end": v(43.87, -16.86) * mm});
            skArc(sketch, "E200.MirrorCS", {"start": v(16.86, -43.87) * mm, "mid": v(17.99, -43.42) * mm, "end": v(19.1, -42.95) * mm});
            skLineSegment(sketch, "E201.MirrorCS", {"start": v(13.45, -39.61) * mm, "end": v(12.47, -44.28) * mm});
            skLineSegment(sketch, "E202.MirrorCS", {"start": v(-46.43, -7.33) * mm, "end": v(-42.96, -8.55) * mm});
            skLineSegment(sketch, "E203.MirrorCS", {"start": v(-14.08, -41.48) * mm, "end": v(-16.86, -43.87) * mm});
            skArc(sketch, "E204.MirrorCS", {"start": v(36.13, -28.47) * mm, "mid": v(36.5, -28) * mm, "end": v(36.85, -27.54) * mm});
            skLineSegment(sketch, "E205.MirrorCS", {"start": v(-36.42, -24.33) * mm, "end": v(-38.01, -27.64) * mm});
            skLineSegment(sketch, "E206.MirrorCS", {"start": v(-41.75, -2.74) * mm, "end": v(-45.68, -5.42) * mm});
            skLineSegment(sketch, "E207.MirrorCS", {"start": v(-43.7, -2.86) * mm, "end": v(-46.74, -4.94) * mm});
            skLineSegment(sketch, "E208.MirrorCS", {"start": v(-46.99, -1.2) * mm, "end": v(-43.7, -2.86) * mm});
            skArc(sketch, "E209.MirrorCS", {"start": v(-4.94, -46.74) * mm, "mid": v(-6.13, -46.6) * mm, "end": v(-7.33, -46.43) * mm});
            skArc(sketch, "E210.MirrorCS", {"start": v(-11, -45.7) * mm, "mid": v(-12.16, -45.4) * mm, "end": v(-13.33, -45.07) * mm});
            skArc(sketch, "E211.MirrorCS", {"start": v(-16.86, -43.87) * mm, "mid": v(-17.99, -43.42) * mm, "end": v(-19.1, -42.95) * mm});
            skLineSegment(sketch, "E212.MirrorCS", {"start": v(-31.45, -27.58) * mm, "end": v(-32.94, -32.1) * mm});
            skLineSegment(sketch, "E213.MirrorCS", {"start": v(-42.27, -18.14) * mm, "end": v(-37.52, -18.5) * mm});
            skLineSegment(sketch, "E214.MirrorCS", {"start": v(-32.93, -28.88) * mm, "end": v(-34.08, -32.37) * mm});
            skLineSegment(sketch, "E215.MirrorCS", {"start": v(-40.09, -24.54) * mm, "end": v(-36.42, -24.33) * mm});
            skLineSegment(sketch, "E216.MirrorCS", {"start": v(-39.28, -19.37) * mm, "end": v(-41.3, -22.45) * mm});
            skLineSegment(sketch, "E217.MirrorCS", {"start": v(-42.95, -19.1) * mm, "end": v(-39.28, -19.37) * mm});
            skLineSegment(sketch, "E218.MirrorCS", {"start": v(-41.48, -14.08) * mm, "end": v(-43.87, -16.86) * mm});
            skLineSegment(sketch, "E219.MirrorCS", {"start": v(-45.07, -13.33) * mm, "end": v(-41.48, -14.08) * mm});
            skLineSegment(sketch, "E220.MirrorCS", {"start": v(-42.96, -8.55) * mm, "end": v(-45.7, -11) * mm});
            skLineSegment(sketch, "E221.MirrorCS", {"start": v(41.48, -14.08) * mm, "end": v(43.87, -16.86) * mm});
            skLineSegment(sketch, "E222.MirrorCS", {"start": v(44.28, -12.47) * mm, "end": v(39.61, -13.45) * mm});
            skLineSegment(sketch, "E223.MirrorCS", {"start": v(-14.08, -41.48) * mm, "end": v(-13.33, -45.07) * mm});
            skLineSegment(sketch, "E224.MirrorCS", {"start": v(36.42, -24.33) * mm, "end": v(38.01, -27.64) * mm});
            skArc(sketch, "E225.MirrorCS", {"start": v(22.5, -40.13) * mm, "mid": v(23, -39.84) * mm, "end": v(23.5, -39.54) * mm});
            skLineSegment(sketch, "E226.MirrorCS", {"start": v(8.55, -42.96) * mm, "end": v(7.33, -46.43) * mm});
            skLineSegment(sketch, "E227.MirrorCS", {"start": v(42.96, -8.55) * mm, "end": v(45.7, -11) * mm});
            skArc(sketch, "E228.MirrorCS", {"start": v(-36.54, -29.56) * mm, "mid": v(-37.29, -28.61) * mm, "end": v(-38.01, -27.64) * mm});
            skLineSegment(sketch, "E229.MirrorCS", {"start": v(-28.88, -32.93) * mm, "end": v(-32.37, -34.08) * mm});
            skLineSegment(sketch, "E230.MirrorCS", {"start": v(31.45, -27.58) * mm, "end": v(32.94, -32.1) * mm});
            skArc(sketch, "E231.MirrorCS", {"start": v(22.45, -41.3) * mm, "mid": v(23.5, -40.7) * mm, "end": v(24.54, -40.09) * mm});
            skArc(sketch, "E232.MirrorCS", {"start": v(32.37, -34.08) * mm, "mid": v(33.23, -33.23) * mm, "end": v(34.08, -32.37) * mm});
            skLineSegment(sketch, "E233.MirrorCS", {"start": v(-8.55, -42.96) * mm, "end": v(-11, -45.7) * mm});
            skLineSegment(sketch, "E234.MirrorCS", {"start": v(-13.45, -39.61) * mm, "end": v(-12.47, -44.28) * mm});
            skArc(sketch, "E235.MirrorCS", {"start": v(45.07, -13.33) * mm, "mid": v(45.4, -12.16) * mm, "end": v(45.7, -11) * mm});
            skLineSegment(sketch, "E236.MirrorCS", {"start": v(14.08, -41.48) * mm, "end": v(16.86, -43.87) * mm});
            skLineSegment(sketch, "E237.MirrorCS", {"start": v(18.5, -37.52) * mm, "end": v(18.14, -42.27) * mm});
            skLineSegment(sketch, "E238.MirrorCS", {"start": v(-39.61, -13.45) * mm, "end": v(-42.72, -17.06) * mm});
            skLineSegment(sketch, "E239.MirrorCS", {"start": v(-27.58, -31.45) * mm, "end": v(-32.1, -32.94) * mm});
            skArc(sketch, "E240.MirrorCS", {"start": v(-32.37, -34.08) * mm, "mid": v(-33.23, -33.23) * mm, "end": v(-34.08, -32.37) * mm});
            skLineSegment(sketch, "E241.MirrorCS", {"start": v(-28.88, -32.93) * mm, "end": v(-29.56, -36.54) * mm});
            skLineSegment(sketch, "E242.MirrorCS", {"start": v(23.24, -34.78) * mm, "end": v(23.5, -39.54) * mm});
            skLineSegment(sketch, "E243.MirrorCS", {"start": v(42.27, -18.14) * mm, "end": v(37.52, -18.5) * mm});
            skLineSegment(sketch, "E244.MirrorCS", {"start": v(13.45, -39.61) * mm, "end": v(17.06, -42.72) * mm});
            skArc(sketch, "E245.MirrorCS", {"start": v(27.64, -38.01) * mm, "mid": v(28.61, -37.29) * mm, "end": v(29.56, -36.54) * mm});
            skLineSegment(sketch, "E246.MirrorCS", {"start": v(8.16, -41.03) * mm, "end": v(6.59, -45.53) * mm});
            skLineSegment(sketch, "E247.MirrorCS", {"start": v(-2.74, -41.75) * mm, "end": v(-5.42, -45.68) * mm});
            skLineSegment(sketch, "E248.MirrorCS", {"start": v(45.07, -13.33) * mm, "end": v(41.48, -14.08) * mm});
            skLineSegment(sketch, "E249.MirrorCS", {"start": v(46.99, -1.2) * mm, "end": v(43.7, -2.86) * mm});
            skLineSegment(sketch, "E250.MirrorCS", {"start": v(-2.86, -43.7) * mm, "end": v(-1.2, -46.99) * mm});
            skLineSegment(sketch, "E251.MirrorCS", {"start": v(46, -0.59) * mm, "end": v(41.75, -2.74) * mm});
            skLineSegment(sketch, "E252.MirrorCS", {"start": v(36.54, -29.56) * mm, "end": v(32.93, -28.88) * mm});
            skLineSegment(sketch, "E253.MirrorCS", {"start": v(-36.13, -28.47) * mm, "end": v(-31.45, -27.58) * mm});
            skLineSegment(sketch, "E254.MirrorCS", {"start": v(-46, -0.59) * mm, "end": v(-41.75, -2.74) * mm});
            skLineSegment(sketch, "E255.MirrorCS", {"start": v(2.86, -43.7) * mm, "end": v(1.2, -46.99) * mm});
            skLineSegment(sketch, "E256.MirrorCS", {"start": v(-8.16, -41.03) * mm, "end": v(-11.34, -44.58) * mm});
            skLineSegment(sketch, "E257.MirrorCS", {"start": v(8.16, -41.03) * mm, "end": v(11.34, -44.58) * mm});
            skLineSegment(sketch, "E258.MirrorCS", {"start": v(-36.54, -29.56) * mm, "end": v(-32.93, -28.88) * mm});
            skLineSegment(sketch, "E259.MirrorCS", {"start": v(45.53, -6.59) * mm, "end": v(41.03, -8.16) * mm});
            skLineSegment(sketch, "E260.MirrorCS", {"start": v(36.13, -28.47) * mm, "end": v(31.45, -27.58) * mm});
            skLineSegment(sketch, "E261.MirrorCS", {"start": v(2.74, -41.75) * mm, "end": v(0.59, -46) * mm});
            skLineSegment(sketch, "E262.MirrorCS", {"start": v(-45.53, -6.59) * mm, "end": v(-41.03, -8.16) * mm});
            skSolve(sketch);
        }
        {
            var Q0;
            Q0=makeQuery(id+"F1.imprint","IMPRINT",FACE,{"disambiguationData":[TD([[makeQuery(id+"F1.imprint","IMPRINT",EDGE,{"derivedFrom":sQuery(id+"F1.wireOp",EDGE,"E40.0")}),-1.0]])]});
            extrude(context, id + "F2", {"entities" : qUnion([Q0]), "endBound" : BoundingType.SYMMETRIC, "depth" : 10.2 * mm, "offsetDistance" : 25 * mm});
        }
    });
